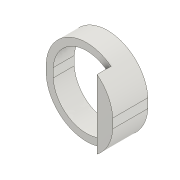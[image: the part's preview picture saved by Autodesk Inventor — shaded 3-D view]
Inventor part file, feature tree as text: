
AUTODESK INVENTOR PART (.ipt)
format: ipt  version: 2020.3 (Build 243373010, 373A)  size: 130,048 bytes
history: native  units: mm
features: extrude x2, sketch x2, fillet x1, projected_geometry x1
ambient origin geometry x8: Origin, YZ Plane, XZ Plane, XY Plane, X Axis, Y Axis, Z Axis, Center Point
bodies: Solid1 (feature_tree)
feature tree (6):
  extrude  "Extrusion1"  Depth=15.0mm TaperAngle=0.0deg
  extrude  "Extrusion2"  Depth=10.0mm TaperAngle=0.0deg
  fillet  "Fillet1"  Radius=2.0mm
  sketch  "Sketch1"  dims[d0=5.0mm d1=15.0mm d2=0.0mm]
  sketch  "Sketch3"  dims[d3=6.207mm d4=10.0mm d5=0.0mm d6=2.0mm]
  projected_geometry  "Projected Loop1"
